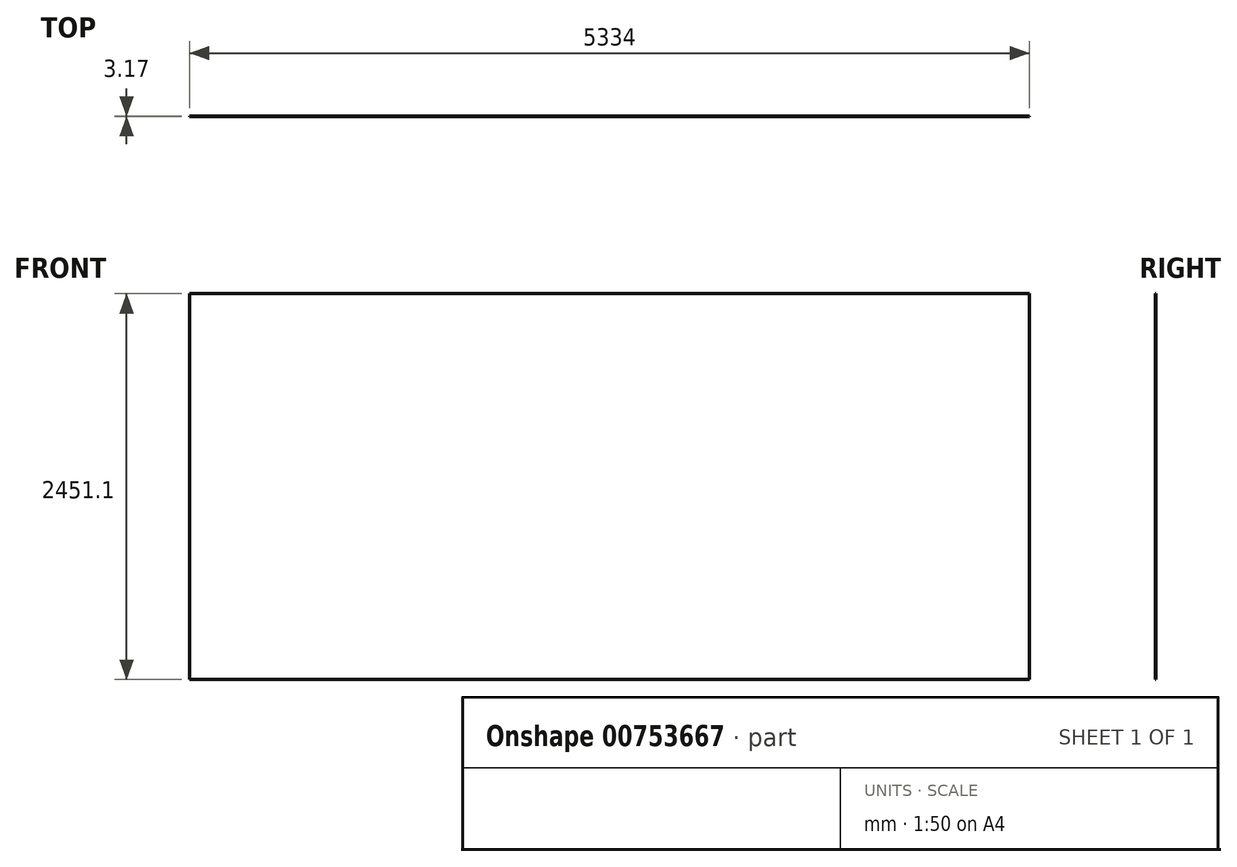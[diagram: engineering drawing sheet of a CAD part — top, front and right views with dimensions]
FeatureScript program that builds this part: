
annotation { "Feature Type Name" : "Feature", "Feature Type Description" : "" }
export const myFeature = defineFeature(function(context is Context, id is Id, definition is map)
    precondition{}
    {
        {
            var Q0;
            Q0=qCreatedBy(makeId("Front.planeOp"),FACE);
            var sketch = newSketch(context, id + "F0", { "sketchPlane" : qUnion([Q0])});
            skLineSegment(sketch, "E0.bottom", {"start": v(0, 0) * mm, "end": v(5334, 0) * mm});
            skLineSegment(sketch, "E0.top", {"start": v(0, 2451.1) * mm, "end": v(5334, 2451.1) * mm});
            skLineSegment(sketch, "E0.left", {"start": v(0, 0) * mm, "end": v(0, 2451.1) * mm});
            skLineSegment(sketch, "E0.right", {"start": v(5334, 0) * mm, "end": v(5334, 2451.1) * mm});
            skSolve(sketch);
        }
        {
            var Q0;
            Q0=makeQuery(id+"F0.imprint","IMPRINT",FACE,{"disambiguationData":[TD([[makeQuery(id+"F0.imprint","IMPRINT",EDGE,{"derivedFrom":sQuery(id+"F0.wireOp",EDGE,"E0.bottom")}),1.0]])]});
            extrude(context, id + "F1", {"entities" : qUnion([Q0]), "oppositeDirection" : true, "depth" : 3.17 * mm, "offsetDistance" : 25.4 * mm});
        }
    });
